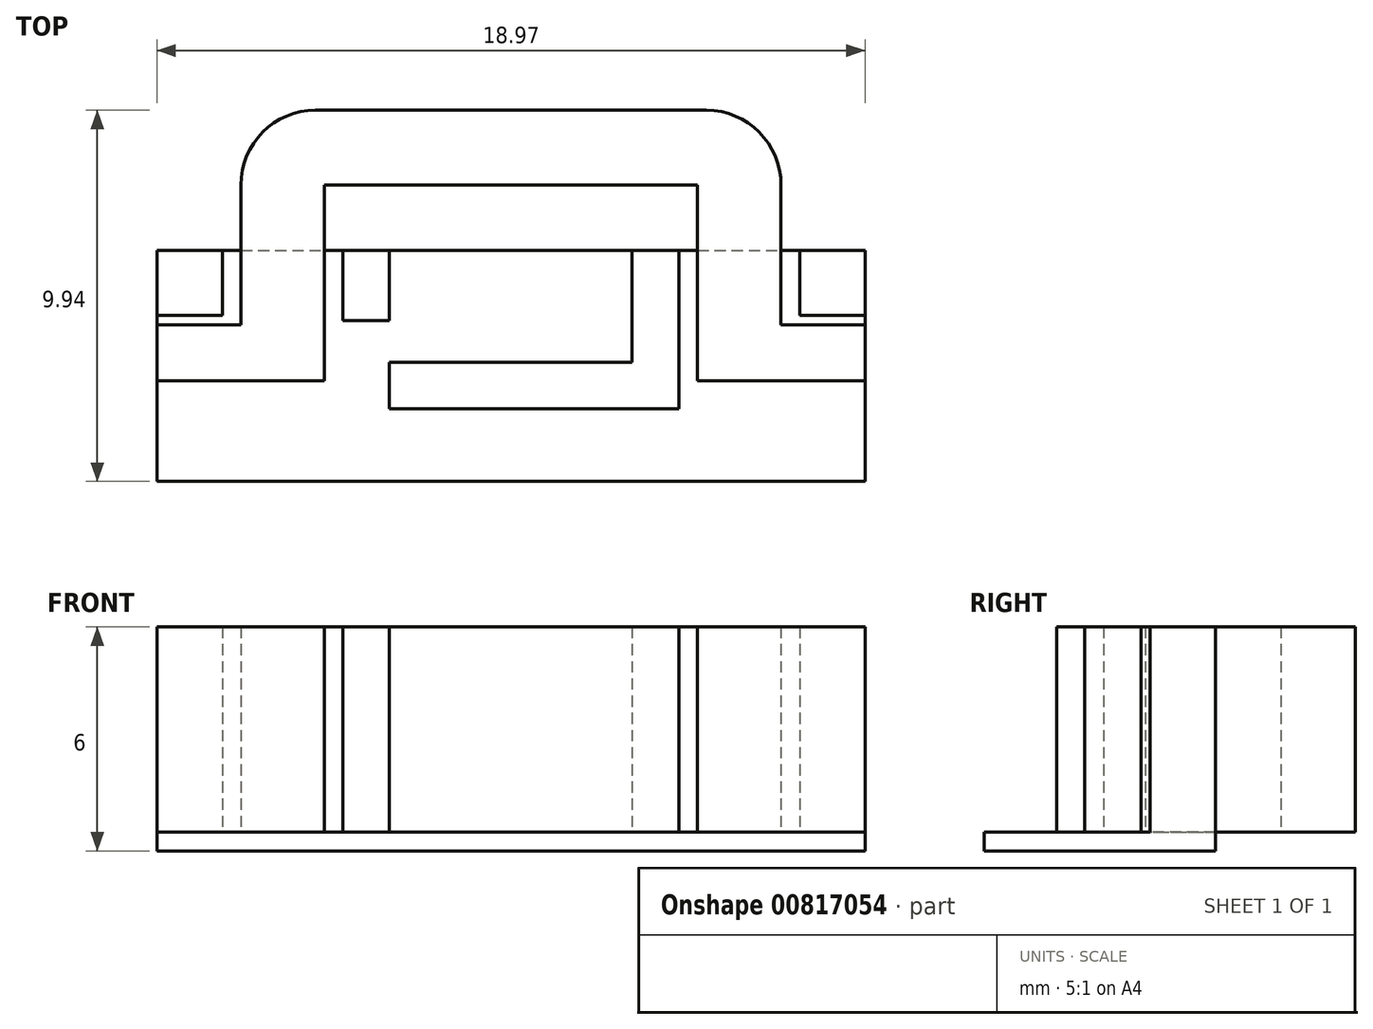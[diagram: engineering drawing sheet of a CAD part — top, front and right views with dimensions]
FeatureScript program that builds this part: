
annotation { "Feature Type Name" : "Feature", "Feature Type Description" : "" }
export const myFeature = defineFeature(function(context is Context, id is Id, definition is map)
    precondition{}
    {
        {
            var Q0;
            Q0=qCreatedBy(makeId("Top.planeOp"),FACE);
            var sketch = newSketch(context, id + "F0", { "sketchPlane" : qUnion([Q0])});
            skLineSegment(sketch, "E0.bottom", {"start": v(-41.94, 27.93) * mm, "end": v(-35.44, 27.93) * mm});
            skLineSegment(sketch, "E0.top", {"start": v(-41.94, 24.93) * mm, "end": v(-35.44, 24.93) * mm});
            skLineSegment(sketch, "E0.left", {"start": v(-41.94, 27.93) * mm, "end": v(-41.94, 24.93) * mm});
            skLineSegment(sketch, "E0.right", {"start": v(-35.44, 27.93) * mm, "end": v(-35.44, 24.93) * mm});
            skLineSegment(sketch, "E1", {"start": v(-35.44, 27.93) * mm, "end": v(-34.2, 27.93) * mm});
            skLineSegment(sketch, "E2", {"start": v(-34.2, 27.93) * mm, "end": v(-34.2, 23.68) * mm});
            skLineSegment(sketch, "E3", {"start": v(-34.2, 23.68) * mm, "end": v(-41.94, 23.68) * mm});
            skLineSegment(sketch, "E4", {"start": v(-41.94, 23.68) * mm, "end": v(-41.94, 24.93) * mm});
            skLineSegment(sketch, "E5", {"start": v(-41.94, 27.93) * mm, "end": v(-43.2, 27.93) * mm});
            skLineSegment(sketch, "E6", {"start": v(-43.2, 27.93) * mm, "end": v(-43.2, 26.05) * mm});
            skLineSegment(sketch, "E7", {"start": v(-43.2, 26.05) * mm, "end": v(-41.94, 26.05) * mm});
            skSolve(sketch);
        }
        {
            var Q0;
            Q0=makeQuery(id+"F0.imprint","IMPRINT",FACE,{"disambiguationData":[TD([[makeQuery(id+"F0.imprint","IMPRINT",EDGE,{"derivedFrom":sQuery(id+"F0.wireOp",EDGE,"E0.bottom")}),-1.0]])]});
            extrude(context, id + "F1", {"entities" : qUnion([Q0]), "depth" : .5 * mm, "offsetDistance" : 25 * mm});
        }
        {
            var Q0;
            Q0=makeQuery(id+"F0.imprint","IMPRINT",FACE,{"disambiguationData":[TD([[makeQuery(id+"F0.imprint","IMPRINT",EDGE,{"derivedFrom":sQuery(id+"F0.wireOp",EDGE,"E0.top")}),-1.0]])]});
            var Q1;
            {var subQ0=sQuery(id+"F0.wireOp",EDGE,"E5");Q1=makeQuery(id+"F0.imprint","IMPRINT",FACE,{"disambiguationData":[TD([[makeQuery(id+"F0.imprint","IMPRINT",EDGE,{"derivedFrom":subQ0}),1.0]])]});}
            extrude(context, id + "F2", {"entities" : qUnion([Q0, Q1]), "operationType" : NewBodyOperationType.ADD, "depth" : 6 * mm, "offsetDistance" : 25 * mm});
        }
        {
            var Q0;
            Q0=qCreatedBy(makeId("Top.planeOp"),FACE);
            var sketch = newSketch(context, id + "F3", { "sketchPlane" : qUnion([Q0])});
            skLineSegment(sketch, "E8.0", {"start": v(-41.94, 27.93) * mm, "end": v(-35.44, 27.93) * mm});
            skLineSegment(sketch, "E9", {"start": v(-41.94, 27.93) * mm, "end": v(-48.17, 27.93) * mm});
            skLineSegment(sketch, "E10", {"start": v(-48.17, 27.93) * mm, "end": v(-48.17, 21.74) * mm});
            skLineSegment(sketch, "E11", {"start": v(-48.17, 21.74) * mm, "end": v(-35.44, 21.74) * mm});
            skLineSegment(sketch, "E12", {"start": v(-35.44, 21.74) * mm, "end": v(-35.44, 27.93) * mm});
            skLineSegment(sketch, "E13", {"start": v(-35.44, 27.93) * mm, "end": v(-29.2, 27.93) * mm});
            skLineSegment(sketch, "E14", {"start": v(-29.2, 27.93) * mm, "end": v(-29.2, 21.74) * mm});
            skLineSegment(sketch, "E15", {"start": v(-35.44, 21.74) * mm, "end": v(-29.2, 21.74) * mm});
            skSolve(sketch);
        }
        {
            var Q0;
            Q0=makeQuery(id+"F3.imprint","IMPRINT",FACE,{"disambiguationData":[TD([[makeQuery(id+"F3.imprint","IMPRINT",EDGE,{"derivedFrom":sQuery(id+"F3.wireOp",EDGE,"E8.0")}),-1.0]])]});
            var Q1;
            Q1=makeQuery(id+"F3.imprint","IMPRINT",FACE,{"disambiguationData":[TD([[makeQuery(id+"F3.imprint","IMPRINT",EDGE,{"derivedFrom":sQuery(id+"F3.wireOp",EDGE,"E12")}),-1.0]])]});
            var Q2;
            Q2=makeQuery(id+"F1.opExtrude","CAP_FACE",FACE,{"disambiguationData":[OSD([sQuery(id+"F0.wireOp",EDGE,"E0.bottom"),sQuery(id+"F0.wireOp",EDGE,"E0.top"),sQuery(id+"F0.wireOp",EDGE,"E0.left"),sQuery(id+"F0.wireOp",EDGE,"E0.right")])],"isStart":false});
            extrude(context, id + "F4", {"entities" : qUnion([Q0, Q1]), "operationType" : NewBodyOperationType.ADD, "endBound" : BoundingType.UP_TO_SURFACE, "depth" : 25 * mm, "endBoundEntityFace" : qUnion([Q2]), "offsetDistance" : 25 * mm});
        }
        {
            var Q0;
            {var subQ0=sQuery(id+"F0.wireOp",EDGE,"E0.right");var subQ1=sQuery(id+"F0.wireOp",EDGE,"E0.left");var subQ2=sQuery(id+"F0.wireOp",EDGE,"E0.top");var subQ3=sQuery(id+"F0.wireOp",EDGE,"E0.bottom");Q0=makeQuery(id+"F4.boolean.opBoolean","MERGE",FACE,{"derivedFrom":[makeQuery(id+"F1.opExtrude","CAP_FACE",FACE,{"disambiguationData":[OSD([subQ3,subQ2,subQ1,subQ0])],"isStart":false}),makeQuery(id+"F4.opExtrude","CAP_FACE",FACE,{"disambiguationData":[OSD([subQ3,subQ2,subQ1,subQ0])],"isStart":false})]});}
            var sketch = newSketch(context, id + "F5", { "sketchPlane" : qUnion([Q0])});
            skLineSegment(sketch, "E16.bottom", {"start": v(-48.17, 27.93) * mm, "end": v(-46.42, 27.93) * mm});
            skLineSegment(sketch, "E16.top", {"start": v(-48.17, 26.18) * mm, "end": v(-46.42, 26.18) * mm});
            skLineSegment(sketch, "E16.left", {"start": v(-48.17, 27.93) * mm, "end": v(-48.17, 26.18) * mm});
            skLineSegment(sketch, "E16.right", {"start": v(-46.42, 27.93) * mm, "end": v(-46.42, 26.18) * mm});
            skLineSegment(sketch, "E17.bottom", {"start": v(-29.2, 27.93) * mm, "end": v(-30.95, 27.93) * mm});
            skLineSegment(sketch, "E17.top", {"start": v(-29.2, 26.18) * mm, "end": v(-30.95, 26.18) * mm});
            skLineSegment(sketch, "E17.left", {"start": v(-29.2, 27.93) * mm, "end": v(-29.2, 26.18) * mm});
            skLineSegment(sketch, "E17.right", {"start": v(-30.95, 27.93) * mm, "end": v(-30.95, 26.18) * mm});
            skSolve(sketch);
        }
        {
            var Q0;
            Q0=makeQuery(id+"F5.imprint","IMPRINT",FACE,{"disambiguationData":[TD([[makeQuery(id+"F5.imprint","IMPRINT",EDGE,{"derivedFrom":sQuery(id+"F5.wireOp",EDGE,"E16.bottom")}),-1.0]])]});
            var Q1;
            Q1=makeQuery(id+"F5.imprint","IMPRINT",FACE,{"disambiguationData":[TD([[makeQuery(id+"F5.imprint","IMPRINT",EDGE,{"derivedFrom":sQuery(id+"F5.wireOp",EDGE,"E17.bottom")}),-1.0]])]});
            var Q2;
            Q2=makeQuery(id+"F2.opExtrude","CAP_FACE",FACE,{"disambiguationData":[OSD([sQuery(id+"F0.wireOp",EDGE,"E0.left"),sQuery(id+"F0.wireOp",EDGE,"E5"),sQuery(id+"F0.wireOp",EDGE,"E6"),sQuery(id+"F0.wireOp",EDGE,"E7")])],"isStart":false});
            extrude(context, id + "F6", {"entities" : qUnion([Q0, Q1]), "operationType" : NewBodyOperationType.ADD, "endBound" : BoundingType.UP_TO_SURFACE, "depth" : 25 * mm, "endBoundEntityFace" : qUnion([Q2]), "offsetDistance" : 25 * mm});
        }
        {
            var Q0;
            {var subQ0=sQuery(id+"F0.wireOp",EDGE,"E0.right");var subQ1=sQuery(id+"F0.wireOp",EDGE,"E0.left");var subQ2=sQuery(id+"F0.wireOp",EDGE,"E0.top");var subQ3=sQuery(id+"F0.wireOp",EDGE,"E0.bottom");Q0=makeQuery(id+"F4.boolean.opBoolean","MERGE",FACE,{"derivedFrom":[makeQuery(id+"F1.opExtrude","CAP_FACE",FACE,{"disambiguationData":[OSD([subQ3,subQ2,subQ1,subQ0])],"isStart":false}),makeQuery(id+"F4.opExtrude","CAP_FACE",FACE,{"disambiguationData":[OSD([subQ3,subQ2,subQ1,subQ0])],"isStart":false})]});}
            var sketch = newSketch(context, id + "F7", { "sketchPlane" : qUnion([Q0])});
            skLineSegment(sketch, "E18", {"start": v(-48.17, 25.93) * mm, "end": v(-45.92, 25.93) * mm});
            skLineSegment(sketch, "E19", {"start": v(-45.92, 25.93) * mm, "end": v(-45.92, 31.68) * mm});
            skLineSegment(sketch, "E20", {"start": v(-45.92, 31.68) * mm, "end": v(-31.45, 31.68) * mm});
            skLineSegment(sketch, "E21", {"start": v(-31.45, 31.68) * mm, "end": v(-31.45, 25.93) * mm});
            skLineSegment(sketch, "E22", {"start": v(-31.45, 25.93) * mm, "end": v(-29.2, 25.93) * mm});
            skLineSegment(sketch, "E23", {"start": v(-48.17, 24.43) * mm, "end": v(-43.7, 24.43) * mm});
            skLineSegment(sketch, "E24", {"start": v(-43.7, 24.43) * mm, "end": v(-43.7, 29.68) * mm});
            skLineSegment(sketch, "E25", {"start": v(-43.7, 29.68) * mm, "end": v(-33.7, 29.68) * mm});
            skLineSegment(sketch, "E26", {"start": v(-33.7, 29.68) * mm, "end": v(-33.7, 24.43) * mm});
            skLineSegment(sketch, "E27", {"start": v(-33.7, 24.43) * mm, "end": v(-29.2, 24.43) * mm});
            skSolve(sketch);
        }
        {
            var Q0;
            {var subQ19=sQuery(id+"F7.wireOp",EDGE,"E20");Q0=makeQuery(id+"F7.imprint","IMPRINT",FACE,{"disambiguationData":[TD([[makeQuery(id+"F7.imprint","IMPRINT",EDGE,{"derivedFrom":subQ19}),-1.0]])]});}
            var Q1;
            {var subQ13=sQuery(id+"F7.wireOp",EDGE,"E18");Q1=makeQuery(id+"F7.imprint","IMPRINT",FACE,{"disambiguationData":[TD([[makeQuery(id+"F7.imprint","IMPRINT",EDGE,{"derivedFrom":subQ13}),-1.0]])]});}
            var Q2;
            {var subQ13=sQuery(id+"F7.wireOp",EDGE,"E22");Q2=makeQuery(id+"F7.imprint","IMPRINT",FACE,{"disambiguationData":[TD([[makeQuery(id+"F7.imprint","IMPRINT",EDGE,{"derivedFrom":subQ13}),-1.0]])]});}
            var Q3;
            Q3=makeQuery(id+"F2.opExtrude","CAP_FACE",FACE,{"disambiguationData":[OSD([sQuery(id+"F0.wireOp",EDGE,"E0.left"),sQuery(id+"F0.wireOp",EDGE,"E5"),sQuery(id+"F0.wireOp",EDGE,"E6"),sQuery(id+"F0.wireOp",EDGE,"E7")])],"isStart":false});
            extrude(context, id + "F8", {"entities" : qUnion([Q0, Q1, Q2]), "endBound" : BoundingType.UP_TO_SURFACE, "depth" : 25 * mm, "endBoundEntityFace" : qUnion([Q3]), "offsetDistance" : 25 * mm});
        }
        {
            var Q0;
            Q0=makeQuery(id+"F8.opExtrude","SWEPT_EDGE",EDGE,{"disambiguationData":[OSD([sQuery(id+"F7.wireOp",EDGE,"E19"),sQuery(id+"F7.wireOp",EDGE,"E20")])]});
            fillet(context, id + "F9", {"entities" : qUnion([Q0]), "radius" : 2 * mm, "tangentPropagation" : true, "allowEdgeOverflow" : false});
        }
        {
            var Q0;
            Q0=makeQuery(id+"F8.opExtrude","SWEPT_EDGE",EDGE,{"disambiguationData":[OSD([sQuery(id+"F7.wireOp",EDGE,"E20"),sQuery(id+"F7.wireOp",EDGE,"E21")])]});
            fillet(context, id + "F10", {"entities" : qUnion([Q0]), "radius" : 2 * mm, "tangentPropagation" : true, "allowEdgeOverflow" : false});
        }
    });
